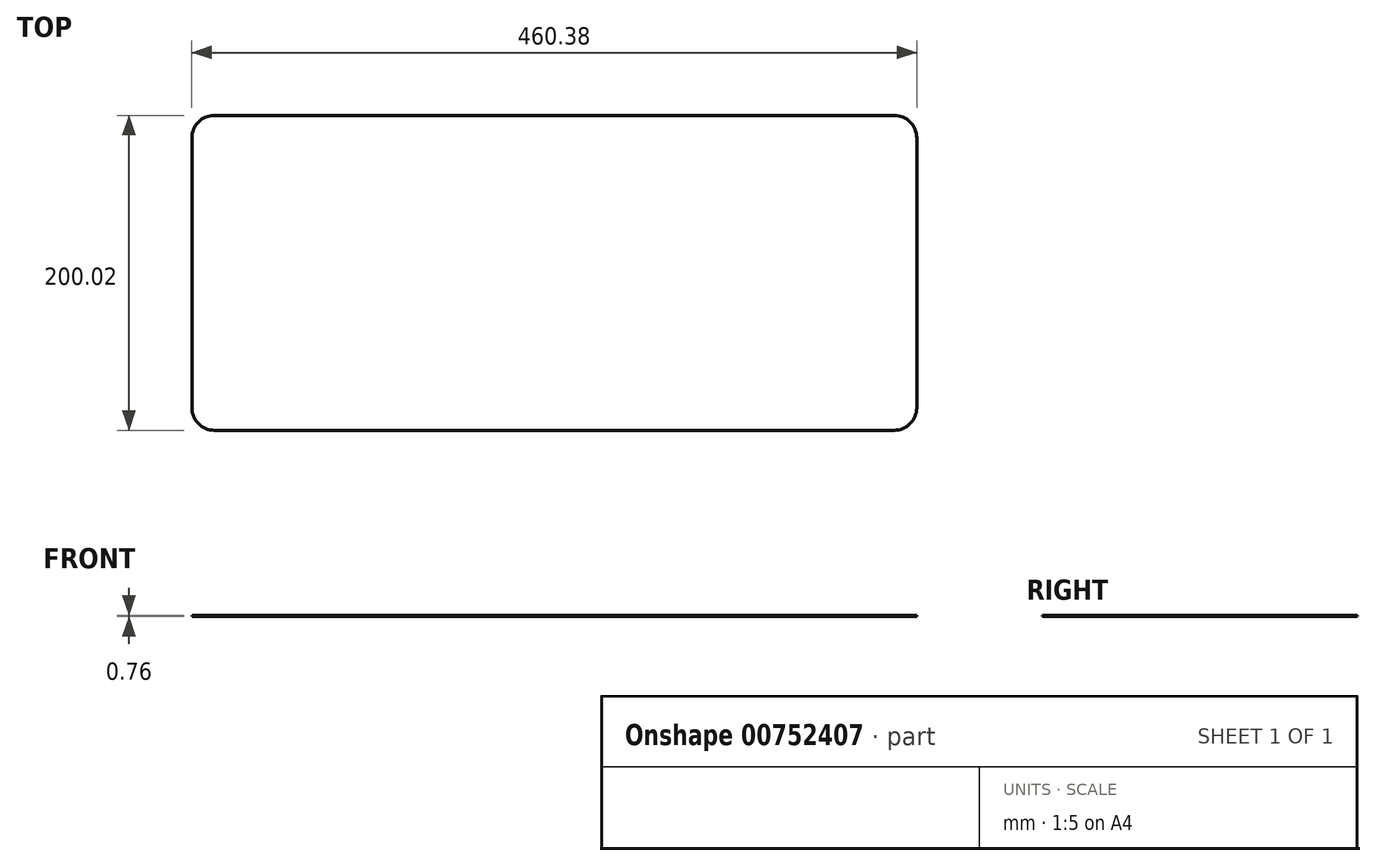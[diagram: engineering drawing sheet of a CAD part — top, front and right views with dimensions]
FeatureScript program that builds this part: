
annotation { "Feature Type Name" : "Feature", "Feature Type Description" : "" }
export const myFeature = defineFeature(function(context is Context, id is Id, definition is map)
    precondition{}
    {
        {
            var Q0;
            Q0=qCreatedBy(makeId("Top.planeOp"),FACE);
            var sketch = newSketch(context, id + "F0", { "sketchPlane" : qUnion([Q0])});
            skPoint(sketch, "E0.middle", {"position": v(0, 0) * mm});
            skPoint(sketch, "E1.orphan", {"position": v(0, 92.08) * mm});
            skPoint(sketch, "E2.end.orphan", {"position": v(0, -92.08) * mm});
            skPoint(sketch, "E3.visualSharp", {"position": v(222.25, 92.08) * mm});
            skPoint(sketch, "E4.visualSharp", {"position": v(6.35, 92.08) * mm});
            skPoint(sketch, "E5.visualSharp", {"position": v(-6.35, 92.08) * mm});
            skPoint(sketch, "E6.visualSharp", {"position": v(-222.25, 92.08) * mm});
            skPoint(sketch, "E7.visualSharp", {"position": v(-222.25, -92.08) * mm});
            skPoint(sketch, "E8.visualSharp", {"position": v(-6.35, -92.08) * mm});
            skPoint(sketch, "E9.visualSharp", {"position": v(6.35, -92.08) * mm});
            skPoint(sketch, "E10.visualSharp", {"position": v(222.25, -92.08) * mm});
            skArc(sketch, "E11.0", {"start": v(230.19, 85.73) * mm, "mid": v(226, 95.83) * mm, "end": v(215.9, 100.01) * mm});
            skLineSegment(sketch, "E11.1", {"start": v(230.19, -85.73) * mm, "end": v(230.19, 85.73) * mm});
            skLineSegment(sketch, "E11.2", {"start": v(215.9, 100.01) * mm, "end": v(-215.9, 100.01) * mm});
            skArc(sketch, "E11.3", {"start": v(215.9, -100.01) * mm, "mid": v(226, -95.83) * mm, "end": v(230.19, -85.73) * mm});
            skArc(sketch, "E11.4", {"start": v(-215.9, 100.01) * mm, "mid": v(-226, 95.83) * mm, "end": v(-230.19, 85.73) * mm});
            skLineSegment(sketch, "E11.5", {"start": v(-230.19, -85.73) * mm, "end": v(-230.19, 85.73) * mm});
            skArc(sketch, "E11.6", {"start": v(-230.19, -85.73) * mm, "mid": v(-226, -95.83) * mm, "end": v(-215.9, -100.01) * mm});
            skLineSegment(sketch, "E11.7", {"start": v(-215.9, -100.01) * mm, "end": v(215.9, -100.01) * mm});
            skSolve(sketch);
        }
        {
            var Q0;
            Q0=makeQuery(id+"F0.imprint","IMPRINT",FACE,{"disambiguationData":[TD([[makeQuery(id+"F0.imprint","IMPRINT",EDGE,{"derivedFrom":sQuery(id+"F0.wireOp",EDGE,"E11.0")}),1.0]])]});
            extrude(context, id + "F1", {"entities" : qUnion([Q0]), "oppositeDirection" : true, "depth" : 0.76 * mm, "offsetDistance" : 25.4 * mm});
        }
    });
